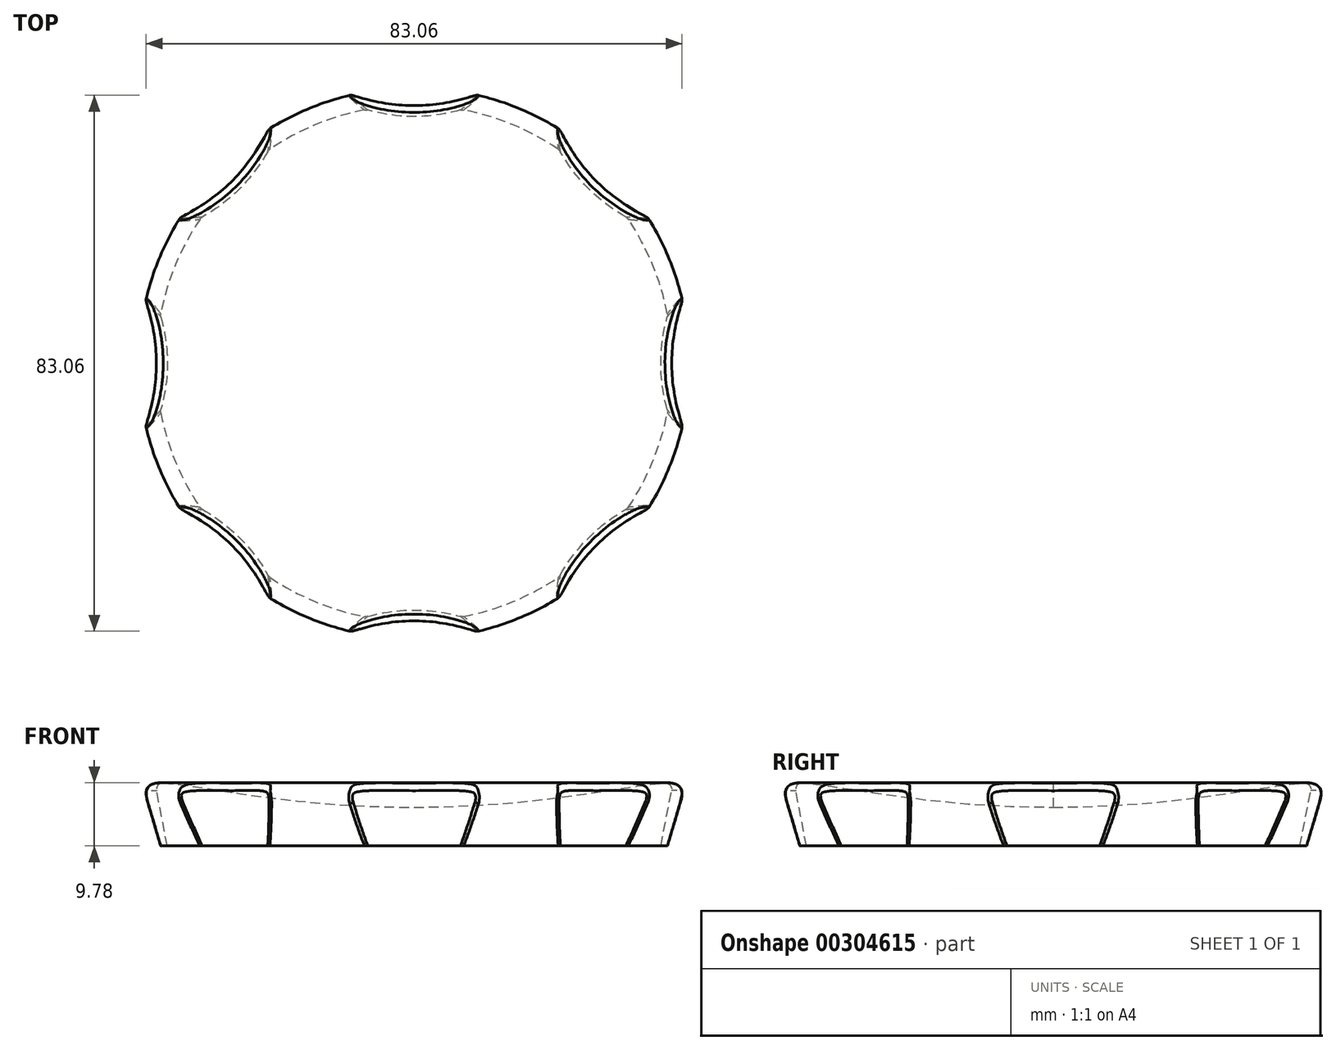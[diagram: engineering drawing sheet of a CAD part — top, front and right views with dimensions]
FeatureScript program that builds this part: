
annotation { "Feature Type Name" : "Feature", "Feature Type Description" : "" }
export const myFeature = defineFeature(function(context is Context, id is Id, definition is map)
    precondition{}
    {
        {
            var Q0;
            Q0=qCreatedBy(makeId("Front.planeOp"),FACE);
            var sketch = newSketch(context, id + "F0", { "sketchPlane" : qUnion([Q0])});
            skLineSegment(sketch, "E0", {"start": v(-40, 0) * mm, "end": v(40, 0) * mm});
            skLineSegment(sketch, "E1", {"start": v(-40, 0) * mm, "end": v(-42.4, 6.58) * mm});
            skPoint(sketch, "E2", {"position": v(0, 0) * mm});
            skFitSpline(sketch, "E3", {"points": [v(-42.4, 6.58) * mm, v(0, 6) * mm], "startDerivative": vector(-8.2, 22.55) * mm, "endDerivative": vector(90, 0) * mm});
            skLineSegment(sketch, "E4", {"start": v(0, 6) * mm, "end": v(0, 0) * mm});
            skLineSegment(sketch, "E5", {"start": v(-42.4, 6.58) * mm, "end": v(-45.13, 14.1) * mm, "construction": true});
            skLineSegment(sketch, "E6", {"start": v(-62.96, -10) * mm, "end": v(-71.52, 13.5) * mm});
            skLineSegment(sketch, "E7", {"start": v(-42.9, 23.91) * mm, "end": v(-71.52, 13.5) * mm});
            skLineSegment(sketch, "E8", {"start": v(-38.06, -0.94) * mm, "end": v(-62.96, -10) * mm});
            skLineSegment(sketch, "E9", {"start": v(-38.06, -0.94) * mm, "end": v(-28.06, -0.94) * mm});
            skLineSegment(sketch, "E10", {"start": v(-38.06, -0.94) * mm, "end": v(-42.9, 23.91) * mm});
            skSolve(sketch);
        }
        {
            var Q0;
            {var subQ0=sQuery(id+"F0.wireOp",EDGE,"E4");Q0=makeQuery(id+"F0.imprint","IMPRINT",FACE,{"disambiguationData":[TD([[makeQuery(id+"F0.imprint","IMPRINT",EDGE,{"derivedFrom":subQ0}),-1.0]])]});}
            var Q1;
            {var subQ0=sQuery(id+"F0.wireOp",EDGE,"E1");Q1=makeQuery(id+"F0.imprint","IMPRINT",FACE,{"disambiguationData":[TD([[makeQuery(id+"F0.imprint","IMPRINT",EDGE,{"derivedFrom":subQ0}),-1.0]])]});}
            var Q2;
            Q2=sQuery(id+"F0.wireOp",EDGE,"E4");
            revolve(context, id + "F1", {"entities" : qUnion([Q0, Q1]), "axis" : qUnion([Q2]), "revolveType" : RevolveType.FULL});
        }
        {
            var Q0;
            {var subQ1=sQuery(id+"F0.wireOp",EDGE,"E1");Q0=makeQuery(id+"F0.imprint","IMPRINT",FACE,{"disambiguationData":[TD([[makeQuery(id+"F0.imprint","IMPRINT",EDGE,{"derivedFrom":subQ1}),1.0]])]});}
            var Q1;
            {var subQ0=sQuery(id+"F0.wireOp",EDGE,"E1");Q1=makeQuery(id+"F0.imprint","IMPRINT",FACE,{"disambiguationData":[TD([[makeQuery(id+"F0.imprint","IMPRINT",EDGE,{"derivedFrom":subQ0}),-1.0]])]});}
            var Q2;
            Q2=sQuery(id+"F0.wireOp",EDGE,"E6");
            revolve(context, id + "F2", {"entities" : qUnion([Q0, Q1]), "axis" : qUnion([Q2]), "revolveType" : RevolveType.FULL});
        }
        {
            var Q0;
            Q0=makeQuery(id+"F2.opRevolve","SWEPT_BODY",BODY,{"disambiguationData":[OSD([sQuery(id+"F0.wireOp",EDGE,"E6"),sQuery(id+"F0.wireOp",EDGE,"E7"),sQuery(id+"F0.wireOp",EDGE,"E8"),sQuery(id+"F0.wireOp",EDGE,"E10")])]});
            var Q1;
            Q1=makeQuery(id+"F1.opRevolve","SWEPT_EDGE",EDGE,{"disambiguationData":[OSD([sQuery(id+"F0.wireOp",EDGE,"E0"),sQuery(id+"F0.wireOp",EDGE,"E1")])]});
            circularPattern(context, id + "F3", {"entities" : qUnion([Q0]), "axis" : qUnion([Q1]), "angle" : 360 * degree, "instanceCount" : 8, "equalSpace" : true});
        }
        {
            var Q0;
            Q0=makeQuery(id+"F3.opPattern","COPY",BODY,{"derivedFrom":makeQuery(id+"F2.opRevolve","SWEPT_BODY",BODY,{"disambiguationData":[OSD([sQuery(id+"F0.wireOp",EDGE,"E6"),sQuery(id+"F0.wireOp",EDGE,"E7"),sQuery(id+"F0.wireOp",EDGE,"E8"),sQuery(id+"F0.wireOp",EDGE,"E10")])]}),"instanceName":"4"});
            var Q1;
            Q1=makeQuery(id+"F3.opPattern","COPY",BODY,{"derivedFrom":makeQuery(id+"F2.opRevolve","SWEPT_BODY",BODY,{"disambiguationData":[OSD([sQuery(id+"F0.wireOp",EDGE,"E6"),sQuery(id+"F0.wireOp",EDGE,"E7"),sQuery(id+"F0.wireOp",EDGE,"E8"),sQuery(id+"F0.wireOp",EDGE,"E10")])]}),"instanceName":"3"});
            var Q2;
            Q2=makeQuery(id+"F3.opPattern","COPY",BODY,{"derivedFrom":makeQuery(id+"F2.opRevolve","SWEPT_BODY",BODY,{"disambiguationData":[OSD([sQuery(id+"F0.wireOp",EDGE,"E6"),sQuery(id+"F0.wireOp",EDGE,"E7"),sQuery(id+"F0.wireOp",EDGE,"E8"),sQuery(id+"F0.wireOp",EDGE,"E10")])]}),"instanceName":"2"});
            var Q3;
            Q3=makeQuery(id+"F3.opPattern","COPY",BODY,{"derivedFrom":makeQuery(id+"F2.opRevolve","SWEPT_BODY",BODY,{"disambiguationData":[OSD([sQuery(id+"F0.wireOp",EDGE,"E6"),sQuery(id+"F0.wireOp",EDGE,"E7"),sQuery(id+"F0.wireOp",EDGE,"E8"),sQuery(id+"F0.wireOp",EDGE,"E10")])]}),"instanceName":"1"});
            var Q4;
            Q4=makeQuery(id+"F2.opRevolve","SWEPT_BODY",BODY,{"disambiguationData":[OSD([sQuery(id+"F0.wireOp",EDGE,"E6"),sQuery(id+"F0.wireOp",EDGE,"E7"),sQuery(id+"F0.wireOp",EDGE,"E8"),sQuery(id+"F0.wireOp",EDGE,"E10")])]});
            var Q5;
            Q5=makeQuery(id+"F3.opPattern","COPY",BODY,{"derivedFrom":makeQuery(id+"F2.opRevolve","SWEPT_BODY",BODY,{"disambiguationData":[OSD([sQuery(id+"F0.wireOp",EDGE,"E6"),sQuery(id+"F0.wireOp",EDGE,"E7"),sQuery(id+"F0.wireOp",EDGE,"E8"),sQuery(id+"F0.wireOp",EDGE,"E10")])]}),"instanceName":"7"});
            var Q6;
            Q6=makeQuery(id+"F3.opPattern","COPY",BODY,{"derivedFrom":makeQuery(id+"F2.opRevolve","SWEPT_BODY",BODY,{"disambiguationData":[OSD([sQuery(id+"F0.wireOp",EDGE,"E6"),sQuery(id+"F0.wireOp",EDGE,"E7"),sQuery(id+"F0.wireOp",EDGE,"E8"),sQuery(id+"F0.wireOp",EDGE,"E10")])]}),"instanceName":"6"});
            var Q7;
            Q7=makeQuery(id+"F3.opPattern","COPY",BODY,{"derivedFrom":makeQuery(id+"F2.opRevolve","SWEPT_BODY",BODY,{"disambiguationData":[OSD([sQuery(id+"F0.wireOp",EDGE,"E6"),sQuery(id+"F0.wireOp",EDGE,"E7"),sQuery(id+"F0.wireOp",EDGE,"E8"),sQuery(id+"F0.wireOp",EDGE,"E10")])]}),"instanceName":"5"});
            var Q8;
            Q8=makeQuery(id+"F1.opRevolve","SWEPT_BODY",BODY,{"disambiguationData":[OSD([sQuery(id+"F0.wireOp",EDGE,"E0"),sQuery(id+"F0.wireOp",EDGE,"E1"),sQuery(id+"F0.wireOp",EDGE,"E3"),sQuery(id+"F0.wireOp",EDGE,"E4")])]});
            booleanBodies(context, id + "F4", {"operationType" : BooleanOperationType.SUBTRACTION, "tools" : qUnion([Q0, Q1, Q2, Q3, Q4, Q5, Q6, Q7]), "targets" : qUnion([Q8])});
        }
        {
            var Q0;
            Q0=makeQuery(id+"F4.opBoolean","INTERSECT",EDGE,{"derivedFrom":[makeQuery(id+"F1.opRevolve","SWEPT_FACE",FACE,{"disambiguationData":[OSD([sQuery(id+"F0.wireOp",EDGE,"E3")])]}),makeQuery(id+"F3.opPattern","COPY",FACE,{"derivedFrom":makeQuery(id+"F2.opRevolve","SWEPT_FACE",FACE,{"disambiguationData":[OSD([sQuery(id+"F0.wireOp",EDGE,"E10")])]}),"instanceName":"1"})]});
            var Q1;
            Q1=makeQuery(id+"F4.opBoolean","INTERSECT",EDGE,{"derivedFrom":[makeQuery(id+"F1.opRevolve","SWEPT_FACE",FACE,{"disambiguationData":[OSD([sQuery(id+"F0.wireOp",EDGE,"E3")])]}),makeQuery(id+"F3.opPattern","COPY",FACE,{"derivedFrom":makeQuery(id+"F2.opRevolve","SWEPT_FACE",FACE,{"disambiguationData":[OSD([sQuery(id+"F0.wireOp",EDGE,"E10")])]}),"instanceName":"2"})]});
            var Q2;
            Q2=makeQuery(id+"F4.opBoolean","INTERSECT",EDGE,{"derivedFrom":[makeQuery(id+"F1.opRevolve","SWEPT_FACE",FACE,{"disambiguationData":[OSD([sQuery(id+"F0.wireOp",EDGE,"E3")])]}),makeQuery(id+"F3.opPattern","COPY",FACE,{"derivedFrom":makeQuery(id+"F2.opRevolve","SWEPT_FACE",FACE,{"disambiguationData":[OSD([sQuery(id+"F0.wireOp",EDGE,"E10")])]}),"instanceName":"3"})]});
            var Q3;
            Q3=makeQuery(id+"F4.opBoolean","INTERSECT",EDGE,{"derivedFrom":[makeQuery(id+"F1.opRevolve","SWEPT_FACE",FACE,{"disambiguationData":[OSD([sQuery(id+"F0.wireOp",EDGE,"E3")])]}),makeQuery(id+"F3.opPattern","COPY",FACE,{"derivedFrom":makeQuery(id+"F2.opRevolve","SWEPT_FACE",FACE,{"disambiguationData":[OSD([sQuery(id+"F0.wireOp",EDGE,"E10")])]}),"instanceName":"4"})]});
            var Q4;
            Q4=makeQuery(id+"F4.opBoolean","INTERSECT",EDGE,{"derivedFrom":[makeQuery(id+"F1.opRevolve","SWEPT_FACE",FACE,{"disambiguationData":[OSD([sQuery(id+"F0.wireOp",EDGE,"E3")])]}),makeQuery(id+"F3.opPattern","COPY",FACE,{"derivedFrom":makeQuery(id+"F2.opRevolve","SWEPT_FACE",FACE,{"disambiguationData":[OSD([sQuery(id+"F0.wireOp",EDGE,"E10")])]}),"instanceName":"5"})]});
            var Q5;
            Q5=makeQuery(id+"F4.opBoolean","INTERSECT",EDGE,{"derivedFrom":[makeQuery(id+"F1.opRevolve","SWEPT_FACE",FACE,{"disambiguationData":[OSD([sQuery(id+"F0.wireOp",EDGE,"E3")])]}),makeQuery(id+"F3.opPattern","COPY",FACE,{"derivedFrom":makeQuery(id+"F2.opRevolve","SWEPT_FACE",FACE,{"disambiguationData":[OSD([sQuery(id+"F0.wireOp",EDGE,"E10")])]}),"instanceName":"6"})]});
            var Q6;
            Q6=makeQuery(id+"F4.opBoolean","INTERSECT",EDGE,{"derivedFrom":[makeQuery(id+"F1.opRevolve","SWEPT_FACE",FACE,{"disambiguationData":[OSD([sQuery(id+"F0.wireOp",EDGE,"E3")])]}),makeQuery(id+"F3.opPattern","COPY",FACE,{"derivedFrom":makeQuery(id+"F2.opRevolve","SWEPT_FACE",FACE,{"disambiguationData":[OSD([sQuery(id+"F0.wireOp",EDGE,"E10")])]}),"instanceName":"7"})]});
            var Q7;
            Q7=makeQuery(id+"F4.opBoolean","INTERSECT",EDGE,{"derivedFrom":[makeQuery(id+"F1.opRevolve","SWEPT_FACE",FACE,{"disambiguationData":[OSD([sQuery(id+"F0.wireOp",EDGE,"E3")])]}),makeQuery(id+"F2.opRevolve","SWEPT_FACE",FACE,{"disambiguationData":[OSD([sQuery(id+"F0.wireOp",EDGE,"E10")])]})]});
            fillet(context, id + "F5", {"entities" : qUnion([Q0, Q1, Q2, Q3, Q4, Q5, Q6, Q7]), "radius" : 1 * mm, "tangentPropagation" : true, "allowEdgeOverflow" : false});
        }
    });
